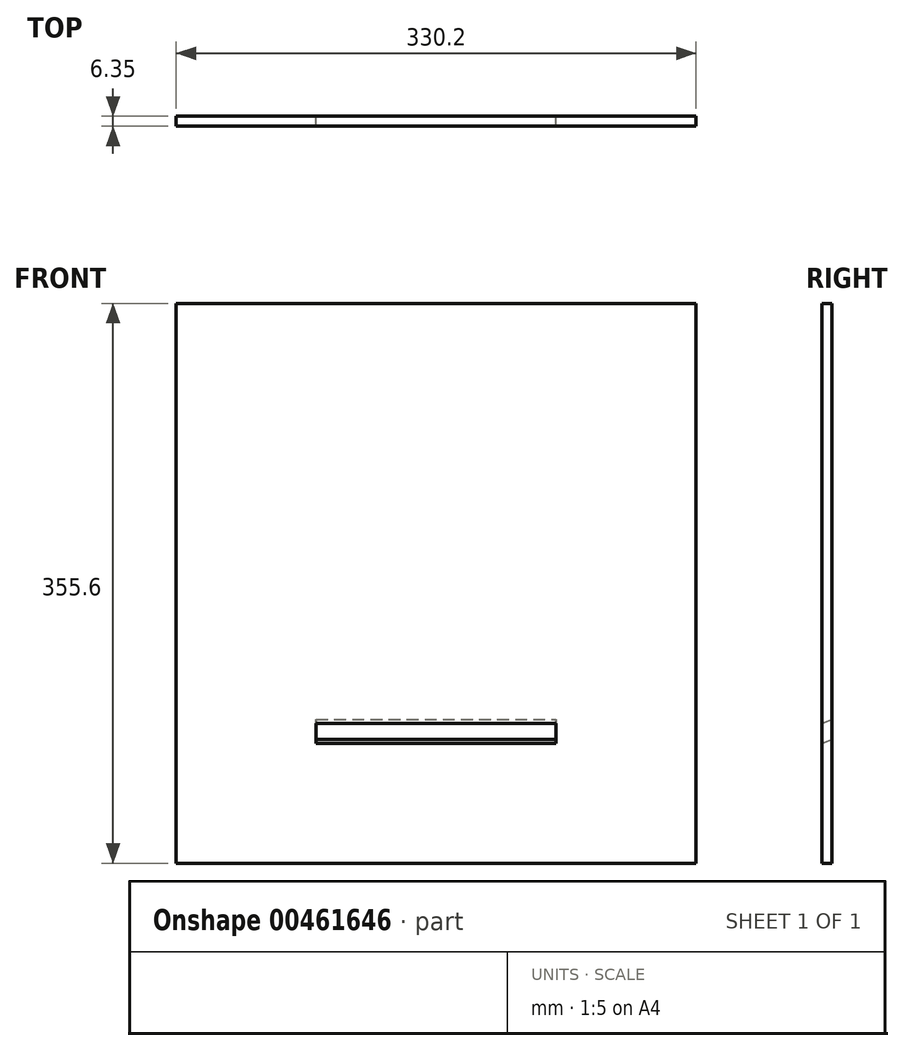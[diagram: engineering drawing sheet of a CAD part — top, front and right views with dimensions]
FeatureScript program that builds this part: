
annotation { "Feature Type Name" : "Feature", "Feature Type Description" : "" }
export const myFeature = defineFeature(function(context is Context, id is Id, definition is map)
    precondition{}
    {
        {
            var Q0;
            Q0=qCreatedBy(makeId("Front.planeOp"),FACE);
            var sketch = newSketch(context, id + "F0", { "sketchPlane" : qUnion([Q0])});
            skLineSegment(sketch, "E0.bottom", {"start": v(165.1, 177.8) * mm, "end": v(-165.1, 177.8) * mm});
            skLineSegment(sketch, "E0.top", {"start": v(165.1, -177.8) * mm, "end": v(-165.1, -177.8) * mm});
            skLineSegment(sketch, "E0.left", {"start": v(165.1, 177.8) * mm, "end": v(165.1, -177.8) * mm});
            skLineSegment(sketch, "E0.right", {"start": v(-165.1, 177.8) * mm, "end": v(-165.1, -177.8) * mm});
            skPoint(sketch, "E0.middle", {"position": v(0, 0) * mm});
            skSolve(sketch);
        }
        {
            var Q0;
            Q0 = qSketchRegion(id + "F0", true);
            extrude(context, id + "F1", {"entities" : qUnion([Q0]), "depth" : 6.35 * mm});
        }
        {
            var Q0;
            Q0=makeQuery(id+"F1.opExtrude","CAP_FACE",FACE,{"disambiguationData":[OSD([sQuery(id+"F0.wireOp",EDGE,"E0.bottom"),sQuery(id+"F0.wireOp",EDGE,"E0.top"),sQuery(id+"F0.wireOp",EDGE,"E0.left"),sQuery(id+"F0.wireOp",EDGE,"E0.right")])],"isStart":false});
            var sketch = newSketch(context, id + "F2", { "sketchPlane" : qUnion([Q0])});
            skLineSegment(sketch, "E1.bottom", {"start": v(-76.2, -88.9) * mm, "end": v(76.2, -88.9) * mm});
            skLineSegment(sketch, "E1.top", {"start": v(-76.2, -101.6) * mm, "end": v(76.2, -101.6) * mm});
            skLineSegment(sketch, "E1.left", {"start": v(-76.2, -88.9) * mm, "end": v(-76.2, -101.6) * mm});
            skLineSegment(sketch, "E1.right", {"start": v(76.2, -88.9) * mm, "end": v(76.2, -101.6) * mm});
            skLineSegment(sketch, "E2", {"start": v(0, 0) * mm, "end": v(0, -177.8) * mm, "construction": true});
            skSolve(sketch);
        }
        {
            var Q0;
            Q0=qCreatedBy(makeId("Right.planeOp"),FACE);
            var sketch = newSketch(context, id + "F3", { "sketchPlane" : qUnion([Q0])});
            skLineSegment(sketch, "E3", {"start": v(-6.35, -101.6) * mm, "end": v(0, -99.29) * mm});
            skLineSegment(sketch, "E4", {"start": v(-6.35, -88.9) * mm, "end": v(0, -86.59) * mm});
            skLineSegment(sketch, "E5.0", {"start": v(-6.35, -88.9) * mm, "end": v(-6.35, -101.6) * mm, "construction": true});
            skSolve(sketch);
        }
        {
            var Q0;
            Q0=makeQuery(id+"F0.imprint","IMPRINT",FACE,{"disambiguationData":[TD([[makeQuery(id+"F0.imprint","IMPRINT",EDGE,{"derivedFrom":sQuery(id+"F0.wireOp",EDGE,"E0.bottom")}),1.0]])]});
            var sketch = newSketch(context, id + "F4", { "sketchPlane" : qUnion([Q0])});
            skLineSegment(sketch, "E6.bottom", {"start": v(-76.2, -86.59) * mm, "end": v(76.2, -86.59) * mm});
            skLineSegment(sketch, "E6.top", {"start": v(-76.2, -99.29) * mm, "end": v(76.2, -99.29) * mm});
            skLineSegment(sketch, "E6.left", {"start": v(-76.2, -86.59) * mm, "end": v(-76.2, -99.29) * mm});
            skLineSegment(sketch, "E6.right", {"start": v(76.2, -86.59) * mm, "end": v(76.2, -99.29) * mm});
            skPoint(sketch, "E7.0", {"position": v(0, -86.59) * mm});
            skPoint(sketch, "E8.0", {"position": v(0, -99.29) * mm});
            skSolve(sketch);
        }
        {
            var Q1;
            Q1=makeQuery(id+"F2.imprint","IMPRINT",FACE,{"disambiguationData":[TD([[makeQuery(id+"F2.imprint","IMPRINT",EDGE,{"derivedFrom":sQuery(id+"F2.wireOp",EDGE,"E1.bottom")}),-1.0]])]});
            var Q2;
            Q2=makeQuery(id+"F4.imprint","IMPRINT",FACE,{"disambiguationData":[TD([[makeQuery(id+"F4.imprint","IMPRINT",EDGE,{"derivedFrom":sQuery(id+"F4.wireOp",EDGE,"E6.bottom")}),-1.0]])]});
            loft(context, id + "F5", {"operationType" : NewBodyOperationType.REMOVE, "sheetProfilesArray" : [{ "sheetProfileEntities" : qUnion([Q1]) }, { "sheetProfileEntities" : qUnion([Q2]) }]});
        }
    });
